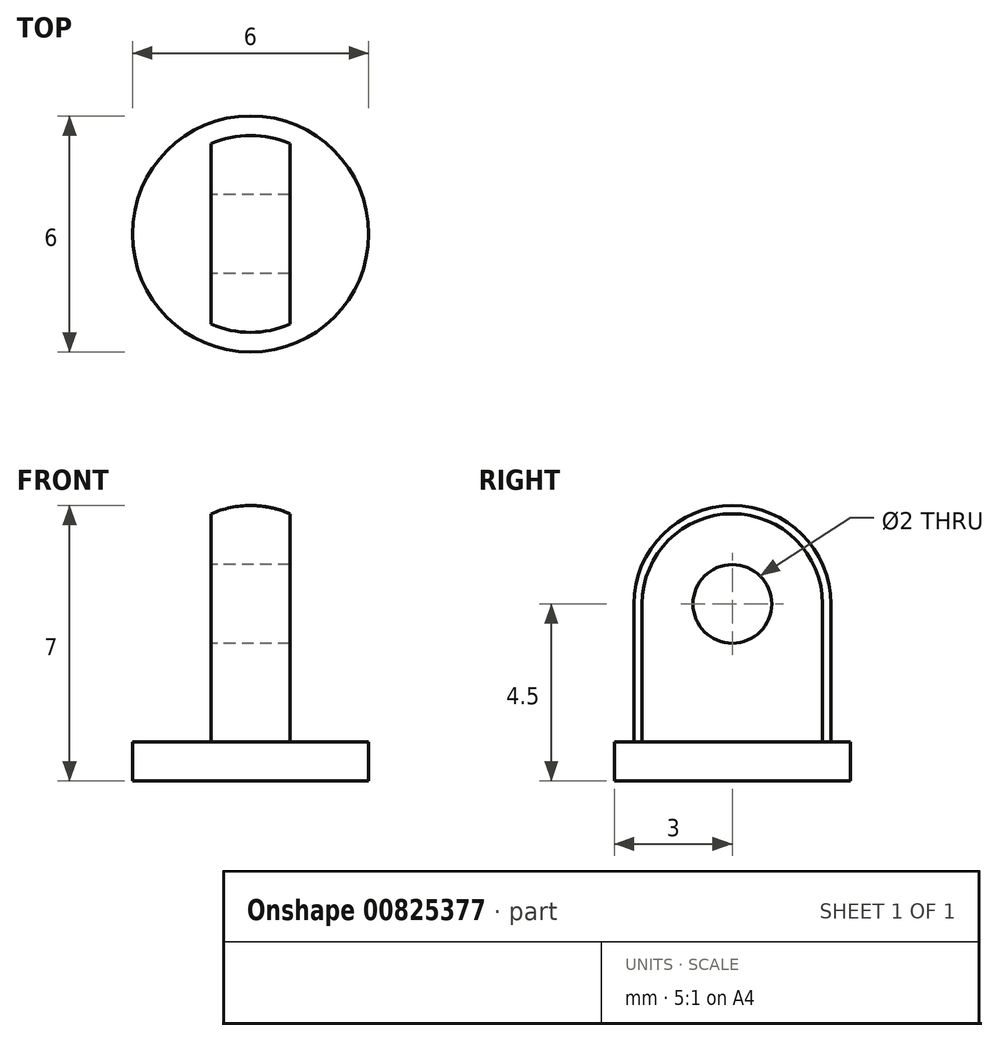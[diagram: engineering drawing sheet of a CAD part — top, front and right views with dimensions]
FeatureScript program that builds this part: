
annotation { "Feature Type Name" : "Feature", "Feature Type Description" : "" }
export const myFeature = defineFeature(function(context is Context, id is Id, definition is map)
    precondition{}
    {
        {
            var Q0;
            Q0=qCreatedBy(makeId("Top.planeOp"),FACE);
            var sketch = newSketch(context, id + "F0", { "sketchPlane" : qUnion([Q0])});
            skCircle(sketch, "E0", {"center": v(0, 0) * mm, "radius": 3 * mm});
            skSolve(sketch);
        }
        {
            var Q0;
            Q0 = qSketchRegion(id + "F0", true);
            extrude(context, id + "F1", {"entities" : qUnion([Q0]), "depth" : 1 * mm, "offsetDistance" : 25 * mm});
        }
        {
            var Q0;
            Q0=makeQuery(id+"F1.opExtrude","CAP_FACE",FACE,{"disambiguationData":[OSD([sQuery(id+"F0.wireOp",EDGE,"E0")])],"isStart":false});
            var sketch = newSketch(context, id + "F2", { "sketchPlane" : qUnion([Q0])});
            skCircle(sketch, "E1", {"center": v(0, 0) * mm, "radius": 2.5 * mm});
            skSolve(sketch);
        }
        {
            var Q0;
            Q0 = qSketchRegion(id + "F2", true);
            extrude(context, id + "F3", {"entities" : qUnion([Q0]), "operationType" : NewBodyOperationType.ADD, "depth" : 6 * mm, "offsetDistance" : 25 * mm});
        }
        {
            var Q0;
            Q0=makeQuery(id+"F3.opExtrude","CAP_FACE",FACE,{"disambiguationData":[OSD([sQuery(id+"F2.wireOp",EDGE,"E1")])],"isStart":false});
            fillet(context, id + "F4", {"entities" : qUnion([Q0]), "radius" : 2.5 * mm, "tangentPropagation" : true, "allowEdgeOverflow" : false});
        }
        {
            var Q0;
            Q0=qCreatedBy(makeId("Front.planeOp"),FACE);
            var sketch = newSketch(context, id + "F5", { "sketchPlane" : qUnion([Q0])});
            skLineSegment(sketch, "E2", {"start": v(0, 0) * mm, "end": v(0, 1) * mm, "construction": true});
            skLineSegment(sketch, "E3", {"start": v(0, 1) * mm, "end": v(1, 1) * mm, "construction": true});
            skLineSegment(sketch, "E4", {"start": v(0, 1) * mm, "end": v(-1, 1) * mm, "construction": true});
            skLineSegment(sketch, "E5.bottom", {"start": v(-1, 1) * mm, "end": v(-2.97, 1) * mm});
            skLineSegment(sketch, "E5.top", {"start": v(-1, 7.62) * mm, "end": v(-2.97, 7.62) * mm});
            skLineSegment(sketch, "E5.left", {"start": v(-1, 1) * mm, "end": v(-1, 7.62) * mm});
            skLineSegment(sketch, "E5.right", {"start": v(-2.97, 1) * mm, "end": v(-2.97, 7.62) * mm});
            skLineSegment(sketch, "E6.bottom", {"start": v(1, 1) * mm, "end": v(3.27, 1) * mm});
            skLineSegment(sketch, "E6.top", {"start": v(1, 7.62) * mm, "end": v(3.27, 7.62) * mm});
            skLineSegment(sketch, "E6.left", {"start": v(1, 1) * mm, "end": v(1, 7.62) * mm});
            skLineSegment(sketch, "E6.right", {"start": v(3.27, 1) * mm, "end": v(3.27, 7.62) * mm});
            skSolve(sketch);
        }
        {
            var Q0;
            Q0 = qSketchRegion(id + "F5", true);
            extrude(context, id + "F6", {"entities" : qUnion([Q0]), "operationType" : NewBodyOperationType.REMOVE, "endBound" : BoundingType.SYMMETRIC, "depth" : 25 * mm, "offsetDistance" : 25 * mm});
        }
        {
            var Q0;
            Q0=makeQuery(id+"F6.boolean.opBoolean","COPY",FACE,{"derivedFrom":makeQuery(id+"F6.opExtrude","SWEPT_FACE",FACE,{"disambiguationData":[OSD([sQuery(id+"F5.wireOp",EDGE,"E5.left")])]})});
            var sketch = newSketch(context, id + "F7", { "sketchPlane" : qUnion([Q0])});
            skCircle(sketch, "E7", {"center": v(0, 4.5) * mm, "radius": 1 * mm});
            skSolve(sketch);
        }
        {
            var Q0;
            Q0 = qSketchRegion(id + "F7", true);
            extrude(context, id + "F8", {"entities" : qUnion([Q0]), "operationType" : NewBodyOperationType.REMOVE, "endBound" : BoundingType.THROUGH_ALL, "oppositeDirection" : true, "depth" : 25 * mm, "offsetDistance" : 25 * mm});
        }
    });
